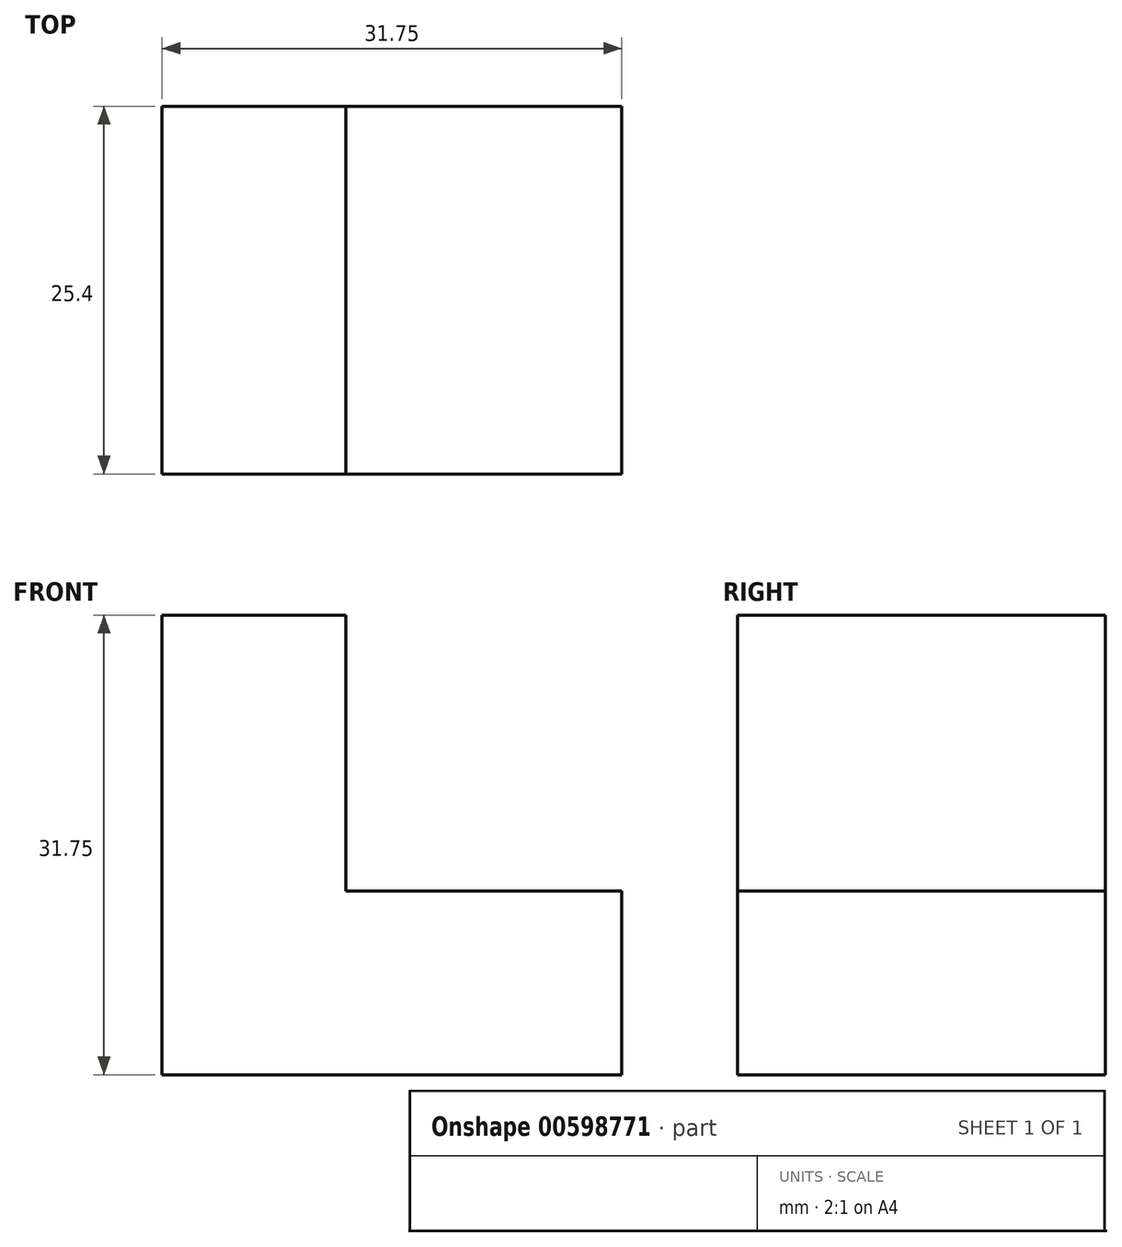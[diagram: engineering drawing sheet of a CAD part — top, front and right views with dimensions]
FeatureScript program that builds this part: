
annotation { "Feature Type Name" : "Feature", "Feature Type Description" : "" }
export const myFeature = defineFeature(function(context is Context, id is Id, definition is map)
    precondition{}
    {
        {
            var Q0;
            Q0=qCreatedBy(makeId("Front.planeOp"),FACE);
            var sketch = newSketch(context, id + "F0", { "sketchPlane" : qUnion([Q0])});
            skLineSegment(sketch, "E0", {"start": v(0, 0) * mm, "end": v(0, 31.75) * mm});
            skLineSegment(sketch, "E1", {"start": v(0, 31.75) * mm, "end": v(12.7, 31.75) * mm});
            skLineSegment(sketch, "E2", {"start": v(12.7, 31.75) * mm, "end": v(12.7, 12.7) * mm});
            skLineSegment(sketch, "E3", {"start": v(12.7, 12.7) * mm, "end": v(31.75, 12.7) * mm});
            skLineSegment(sketch, "E4", {"start": v(31.75, 12.7) * mm, "end": v(31.75, 0) * mm});
            skLineSegment(sketch, "E5", {"start": v(31.75, 0) * mm, "end": v(0, 0) * mm});
            skSolve(sketch);
        }
        {
            var Q0;
            Q0 = qSketchRegion(id + "F0", true);
            extrude(context, id + "F1", {"entities" : qUnion([Q0]), "depth" : 25.4 * mm, "offsetDistance" : 25.4 * mm});
        }
    });
